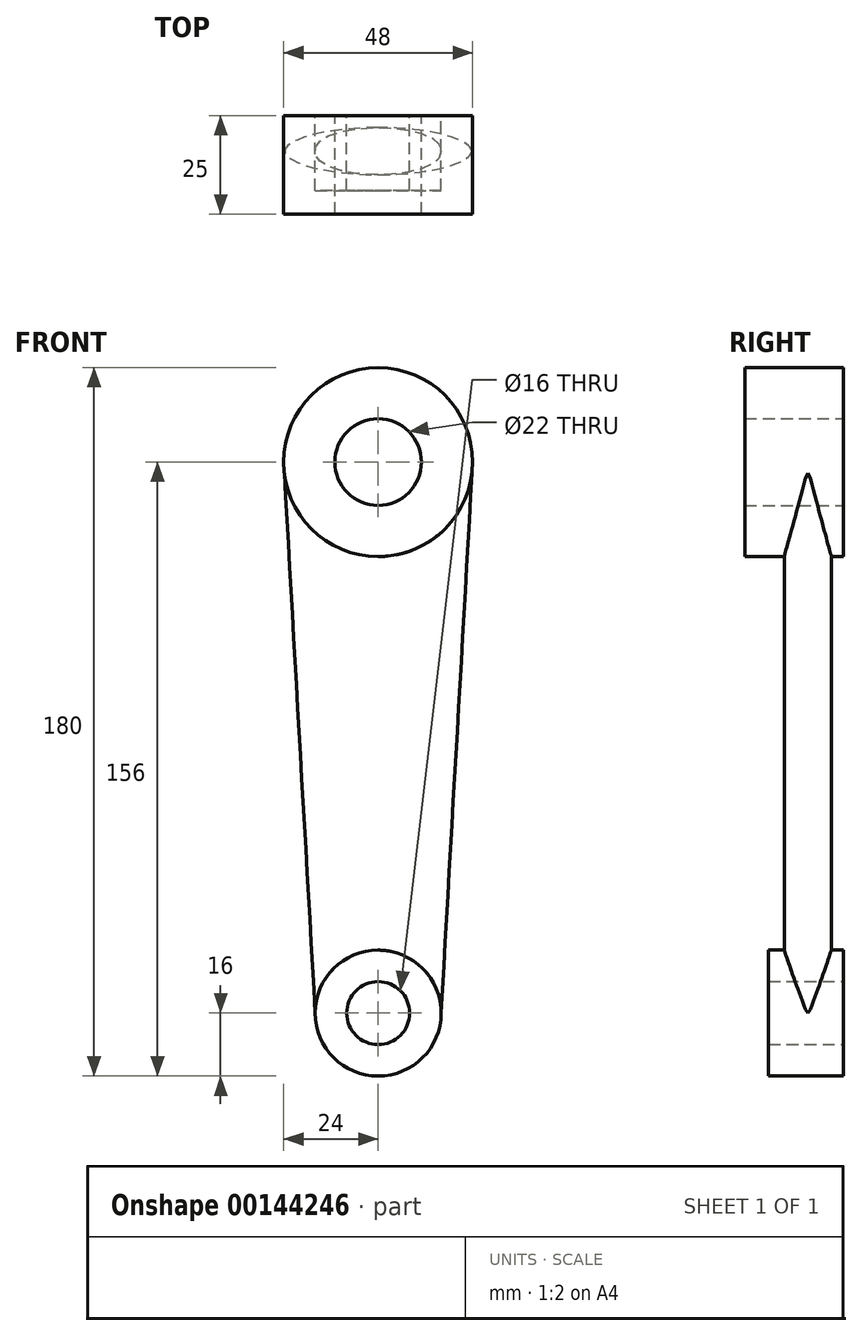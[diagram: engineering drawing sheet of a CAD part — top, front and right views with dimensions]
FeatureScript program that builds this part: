
annotation { "Feature Type Name" : "Feature", "Feature Type Description" : "" }
export const myFeature = defineFeature(function(context is Context, id is Id, definition is map)
    precondition{}
    {
        {
            var Q0;
            Q0=qCreatedBy(makeId("Front.planeOp"),FACE);
            var sketch = newSketch(context, id + "F0", { "sketchPlane" : qUnion([Q0])});
            skCircle(sketch, "E0", {"center": v(0, 140) * mm, "radius": 11 * mm});
            skCircle(sketch, "E1", {"center": v(0, 140) * mm, "radius": 24 * mm});
            skCircle(sketch, "E2", {"center": v(0, 0) * mm, "radius": 8 * mm});
            skCircle(sketch, "E3", {"center": v(0, 0) * mm, "radius": 16 * mm});
            skSolve(sketch);
        }
        {
            var Q0;
            Q0=makeQuery(id+"F0.imprint","IMPRINT",FACE,{"disambiguationData":[TD([[makeQuery(id+"F0.imprint","IMPRINT",EDGE,{"derivedFrom":sQuery(id+"F0.wireOp",EDGE,"E0")}),-1.0]])]});
            var Q1;
            Q1=makeQuery(id+"F0.imprint","IMPRINT",FACE,{"disambiguationData":[TD([[makeQuery(id+"F0.imprint","IMPRINT",EDGE,{"derivedFrom":sQuery(id+"F0.wireOp",EDGE,"E0")}),1.0]])]});
            extrude(context, id + "F1", {"entities" : qUnion([Q0, Q1]), "depth" : 25 * mm});
        }
        {
            var Q0;
            Q0=makeQuery(id+"F0.imprint","IMPRINT",FACE,{"disambiguationData":[TD([[makeQuery(id+"F0.imprint","IMPRINT",EDGE,{"derivedFrom":sQuery(id+"F0.wireOp",EDGE,"E2")}),-1.0]])]});
            var Q1;
            Q1=makeQuery(id+"F0.imprint","IMPRINT",FACE,{"disambiguationData":[TD([[makeQuery(id+"F0.imprint","IMPRINT",EDGE,{"derivedFrom":sQuery(id+"F0.wireOp",EDGE,"E2")}),1.0]])]});
            extrude(context, id + "F2", {"entities" : qUnion([Q0, Q1]), "depth" : 19 * mm});
        }
        {
            var Q0;
            Q0=qCreatedBy(makeId("Top.planeOp"),FACE);
            var sketch = newSketch(context, id + "F3", { "sketchPlane" : qUnion([Q0])});
            skEllipse(sketch, "E4", {"center": v(0, -9) * mm, "majorRadius": 16 * mm, "minorRadius": 6 * mm, "majorAxis": v(1, 0)});
            skPoint(sketch, "E5", {"position": v(0, -3) * mm});
            skLineSegment(sketch, "E6", {"start": v(16, 0) * mm, "end": v(16, -19) * mm, "construction": true});
            skSolve(sketch);
        }
        {
            var Q0;
            Q0=sQuery(id+"F0.wireOp",VERTEX,"E0.center");
            var Q1;
            Q1=qCreatedBy(makeId("Top.planeOp"),FACE);
            cPlane(context, id + "F4", {"entities" : qUnion([Q0, Q1]), "cplaneType" : CPlaneType.PLANE_POINT, "offset" : 25 * mm, "width" : 150 * mm, "height" : 150 * mm});
        }
        {
            var Q0;
            Q0=qCreatedBy(id+"F4.planeOp",FACE);
            var sketch = newSketch(context, id + "F5", { "sketchPlane" : qUnion([Q0])});
            skEllipse(sketch, "E7", {"center": v(0, -9) * mm, "majorRadius": 24 * mm, "minorRadius": 6 * mm, "majorAxis": v(1, 0)});
            skPoint(sketch, "E8", {"position": v(0, -3) * mm});
            skLineSegment(sketch, "E9", {"start": v(24, 0) * mm, "end": v(24, -25) * mm});
            skLineSegment(sketch, "E10", {"start": v(-24, -25) * mm, "end": v(-24, 0) * mm});
            skLineSegment(sketch, "E11", {"start": v(24, 0) * mm, "end": v(24, -25) * mm, "construction": true});
            skSolve(sketch);
        }
        {
            var Q0;
            Q0=makeQuery(id+"F5.imprint","IMPRINT",FACE,{"disambiguationData":[TD([[makeQuery(id+"F5.imprint","IMPRINT",EDGE,{"derivedFrom":sQuery(id+"F5.wireOp",EDGE,"E7")}),1.0]])]});
            var Q1;
            Q1=makeQuery(id+"F3.imprint","IMPRINT",FACE,{"disambiguationData":[TD([[makeQuery(id+"F3.imprint","IMPRINT",EDGE,{"derivedFrom":sQuery(id+"F3.wireOp",EDGE,"E4")}),1.0]])]});
            loft(context, id + "F6", {"operationType" : NewBodyOperationType.ADD, "sheetProfilesArray" : [{ "sheetProfileEntities" : qUnion([Q0]) }, { "sheetProfileEntities" : qUnion([Q1]) }]});
        }
        {
            var Q0;
            Q0=makeQuery(id+"F0.imprint","IMPRINT",FACE,{"disambiguationData":[TD([[makeQuery(id+"F0.imprint","IMPRINT",EDGE,{"derivedFrom":sQuery(id+"F0.wireOp",EDGE,"E0")}),1.0]])]});
            var Q1;
            Q1=makeQuery(id+"F0.imprint","IMPRINT",FACE,{"disambiguationData":[TD([[makeQuery(id+"F0.imprint","IMPRINT",EDGE,{"derivedFrom":sQuery(id+"F0.wireOp",EDGE,"E2")}),1.0]])]});
            extrude(context, id + "F7", {"entities" : qUnion([Q0, Q1]), "operationType" : NewBodyOperationType.REMOVE, "endBound" : BoundingType.THROUGH_ALL, "depth" : 25 * mm});
        }
    });
